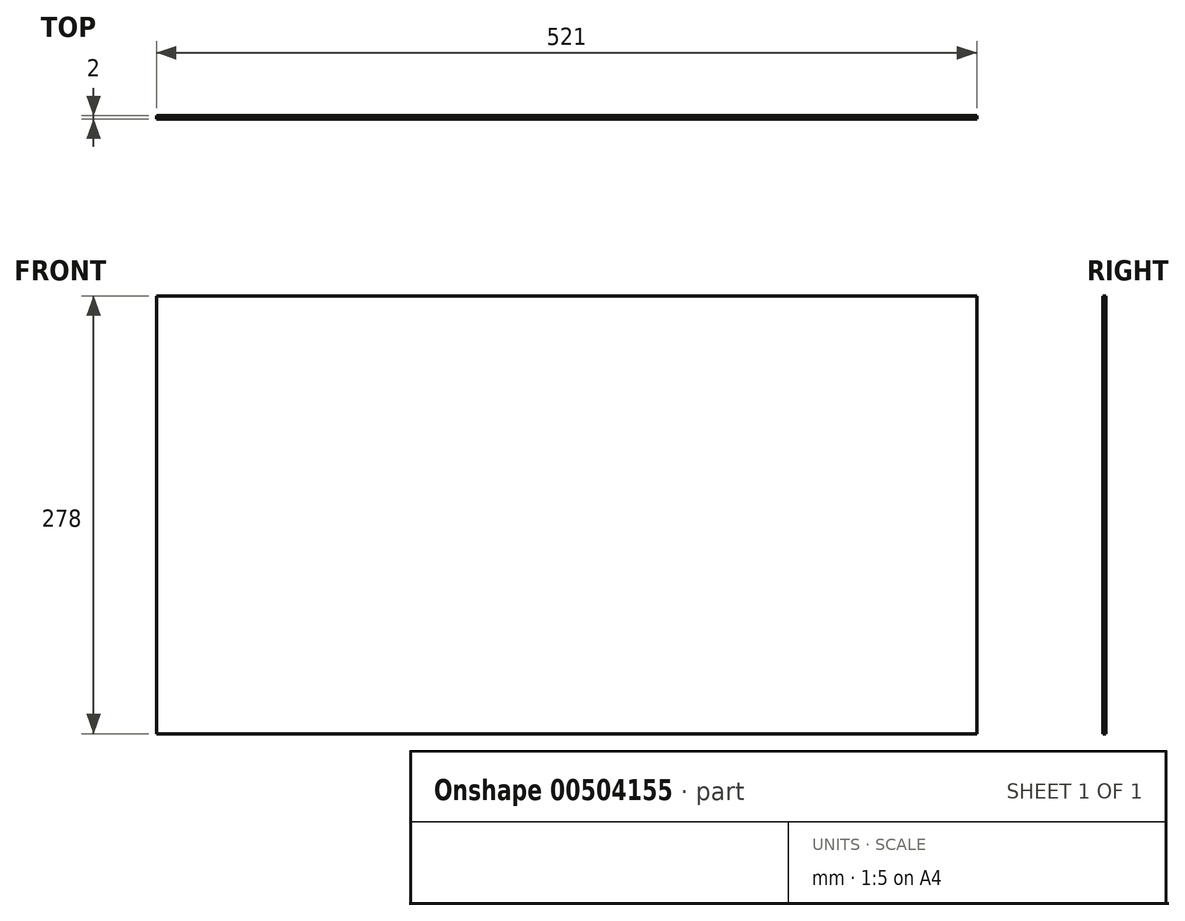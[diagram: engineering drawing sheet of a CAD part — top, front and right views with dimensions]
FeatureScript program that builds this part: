
annotation { "Feature Type Name" : "Feature", "Feature Type Description" : "" }
export const myFeature = defineFeature(function(context is Context, id is Id, definition is map)
    precondition{}
    {
        {
            var Q0;
            Q0=qCreatedBy(makeId("Front.planeOp"),FACE);
            var sketch = newSketch(context, id + "F0", { "sketchPlane" : qUnion([Q0])});
            skLineSegment(sketch, "E0.bottom", {"start": v(260.5, -139) * mm, "end": v(-260.5, -139) * mm});
            skLineSegment(sketch, "E0.top", {"start": v(260.5, 139) * mm, "end": v(-260.5, 139) * mm});
            skLineSegment(sketch, "E0.left", {"start": v(260.5, -139) * mm, "end": v(260.5, 139) * mm});
            skLineSegment(sketch, "E0.right", {"start": v(-260.5, -139) * mm, "end": v(-260.5, 139) * mm});
            skPoint(sketch, "E0.middle", {"position": v(0, 0) * mm});
            skSolve(sketch);
        }
        {
            var Q0;
            Q0=makeQuery(id+"F0.imprint","IMPRINT",FACE,{"disambiguationData":[TD([[makeQuery(id+"F0.imprint","IMPRINT",EDGE,{"derivedFrom":sQuery(id+"F0.wireOp",EDGE,"E0.bottom")}),-1.0]])]});
            extrude(context, id + "F1", {"entities" : qUnion([Q0]), "depth" : 2 * mm, "offsetDistance" : 25 * mm});
        }
    });
